# Revit family: Specialty_Equipment-ToughGate-rev
name_source: partatom
category: Specialty Equipment
units: mm (PartAtom-declared; Revit-internal decimal feet)

## family parameters
Always vertical = Yes
Cut with Voids When Loaded = No
Enable Cutting in Views = No
Maintain Annotation Orientation = No
OmniClass Number = 23.25.40.21
OmniClass Title = Fences
Part Type = Normal
Room Calculation Point = No
Round Connector Dimension = Use Diameter
Shared = No
Work Plane-Based = No

## types (2) — shared parameters
Assembly Code = G2040100
CD_Depth = 0' - 5 1/2"
CD_Drop Pins = Yes
CD_Finish Frame = Metal-Aluminum-Cityscapes-Electric_Black
CD_Height = 6' - 0"
CD_Height Max = 14' - 0"
CD_Height Min = 4' - 0"
CD_Hinge Post = Yes
CD_Jamb Post = Yes
CD_Microsite = https://www.caddetails.com
CD_Panel Height = 5' - 8"
CD_Panel Offset = 0' - 4"
CD_Product Documentation Link = https://9415688.fs1.hubspotusercontent-na1.net
CD_Product Page URL = https://cityscapesinc.com
CD_Requested Height = 6' - 0"
CD_Requested Opening Width = 4' - 0"
CD_Width = 4' - 11"
CD_Width Max = 6' - 0"
CD_Width Min = 1' - 6"
CD_Width Opening = 4' - 0"
CD_Width Panel = 3' - 11 3/4"
Default Elevation = 0' - 0"
Description = Double Post
Manufacturer = CityScapes
Model = ToughGate
URL = https://cityscapesinc.com

## per-type parameters (varying)
| type | CD_Direct Bury | CD_Finish | CD_Left Footing | CD_Right Footing | CD_Support Depth | CD_Surface Mount | Type Comments |
| Direct Bury | Yes | Plastic-PVC-CityScapes-Horizontal-Kona | No | No | 4' - 0" | No | Direct Bury Gate |
| Surface Mount | No | Plastic-PVC-CityScapes-Vertical-Kona | Yes | Yes | 0' - 0" | Yes | Surface Mounted Gate |

## geometry (parser evidence)
native form markers: Sweep x4
no freeform markers — native parametric forms only
